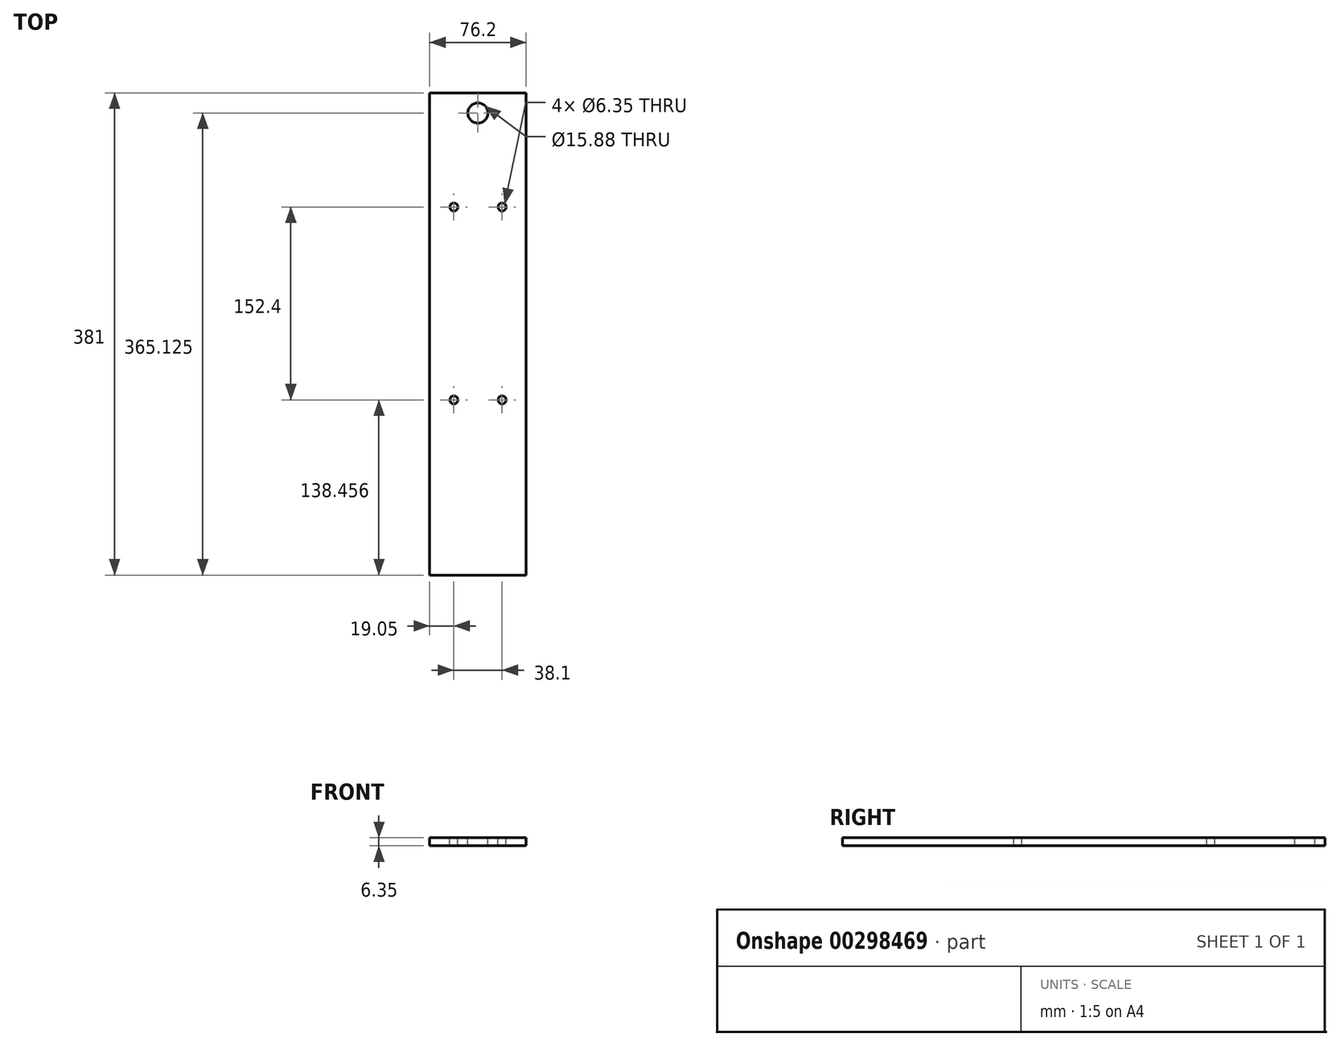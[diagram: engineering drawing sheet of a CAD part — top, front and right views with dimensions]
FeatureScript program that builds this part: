
annotation { "Feature Type Name" : "Feature", "Feature Type Description" : "" }
export const myFeature = defineFeature(function(context is Context, id is Id, definition is map)
    precondition{}
    {
        {
            var Q0;
            Q0=qCreatedBy(makeId("Top.planeOp"),FACE);
            var sketch = newSketch(context, id + "F0", { "sketchPlane" : qUnion([Q0])});
            skLineSegment(sketch, "E0.bottom", {"start": v(0, 0) * mm, "end": v(76.2, 0) * mm});
            skLineSegment(sketch, "E0.top", {"start": v(0, -381) * mm, "end": v(76.2, -381) * mm});
            skLineSegment(sketch, "E0.left", {"start": v(0, 0) * mm, "end": v(0, -381) * mm});
            skLineSegment(sketch, "E0.right", {"start": v(76.2, 0) * mm, "end": v(76.2, -381) * mm});
            skSolve(sketch);
        }
        {
            var Q0;
            Q0 = qSketchRegion(id + "F0", true);
            extrude(context, id + "F1", {"entities" : qUnion([Q0]), "depth" : 6.35 * mm});
        }
        {
            var Q0;
            Q0=makeQuery(id+"F1.opExtrude","CAP_FACE",FACE,{"disambiguationData":[OSD([sQuery(id+"F0.wireOp",EDGE,"E0.bottom"),sQuery(id+"F0.wireOp",EDGE,"E0.top"),sQuery(id+"F0.wireOp",EDGE,"E0.left"),sQuery(id+"F0.wireOp",EDGE,"E0.right")])],"isStart":false});
            var sketch = newSketch(context, id + "F2", { "sketchPlane" : qUnion([Q0])});
            skLineSegment(sketch, "E1", {"start": v(38.1, 0) * mm, "end": v(38.1, -381) * mm, "construction": true});
            skCircle(sketch, "E2", {"center": v(38.1, -15.88) * mm, "radius": 7.94 * mm});
            skCircle(sketch, "E3", {"center": v(19.05, -90.14) * mm, "radius": 3.18 * mm});
            skCircle(sketch, "E4.0.1.0", {"center": v(19.05, -242.54) * mm, "radius": 3.18 * mm});
            skCircle(sketch, "E4.1.0.0", {"center": v(57.15, -90.14) * mm, "radius": 3.18 * mm});
            skCircle(sketch, "E4.1.1.0", {"center": v(57.15, -242.54) * mm, "radius": 3.18 * mm});
            skLineSegment(sketch, "E4.direction1", {"start": v(19.05, -90.14) * mm, "end": v(57.15, -90.14) * mm, "construction": true});
            skLineSegment(sketch, "E4.direction2", {"start": v(19.05, -90.14) * mm, "end": v(19.05, -242.54) * mm, "construction": true});
            skSolve(sketch);
        }
        {
            var Q0;
            Q0 = qSketchRegion(id + "F2", true);
            extrude(context, id + "F3", {"entities" : qUnion([Q0]), "operationType" : NewBodyOperationType.REMOVE, "oppositeDirection" : true, "depth" : 25.4 * mm});
        }
    });
